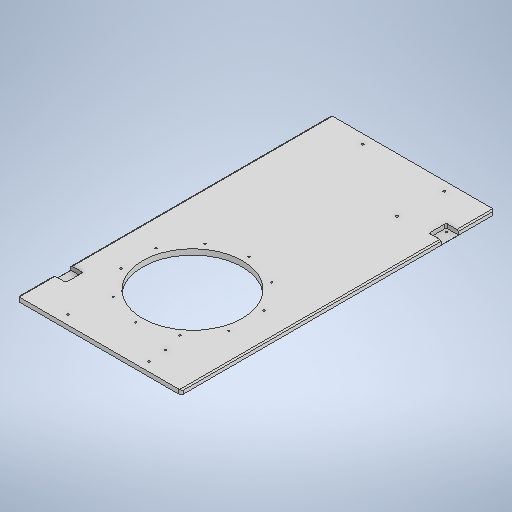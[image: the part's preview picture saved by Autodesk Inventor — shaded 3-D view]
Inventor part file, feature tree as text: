
AUTODESK INVENTOR PART (.ipt)
format: ipt  version: 2025 (Build 290162000, 162)  size: 412,160 bytes
history: native  units: in
note: dims shown in document units (in); Inventor stores cm internally (conversion verified against a paired STEP export)
features: sketch x10, extrude x5, hole x4, chamfer x3, plane x2, fillet x2, pattern_circular x1
ambient origin geometry x8: Origin, YZ Plane, XZ Plane, XY Plane, X Axis, Y Axis, Z Axis, Center Point
bodies: Solid1 (feature_tree)
feature tree (27):
  extrude  "Base Cover"  Depth=27.1654in
  sketch  "Sketch2"  dims[d2=0.4724in d3=0.0in d4=8.0709in]
  extrude  "Cylinder Hole"  Depth=0.4724in
  plane  "Work Plane1"
  hole  "Handle Holes"  [1 undecoded]
  sketch  "Sketch7"  dims[d8=10.6299in d50=5.9055in d55=7.0625in]
  plane  "Work Plane2"
  hole  "Cylinder Mount Holes"  [1 undecoded]
  sketch  "Sketch9"  dims[d57=0.1936in d58=0.1969in d59=0.1575in d60=0.0787in d61=90.0deg d62=0.1969in d63=0.8108in]
  fillet  "Rounded Side Corners"  Radius=7.0625in
  chamfer  "Chamfer1"  Distance=1.063in
  chamfer  "Chamfer2"  Distance=1.063in
  extrude  "Magnet Seats"  Depth=0.315in
  hole  "Magnet Holes"  [1 undecoded]
  chamfer  "Chamfer5"  Distance=3.1102in
  fillet  "Rounded Bottom Corners"  Radius=3.1102in
  extrude  "Extrusion14"  Depth=0.315in
  extrude  "Extrusion15"  Depth=0.0984in TaperAngle=45.0deg
  pattern_circular  "Circular Pattern1"  Angle=45.0deg  [1 undecoded]
  hole  "Hole11"  [1 undecoded]
  sketch  "Sketch1"  dims[d0=14.1732in d1=27.1654in]
  sketch  "Sketch6"  dims[d5=8.6614in d6=0.0in d7=0.0in]
  sketch  "Sketch8"  dims[d56=25.5906in]
  sketch  "Sketch11"  dims[d64=10.3543in]
  sketch  "Sketch18"  dims[d65=10.6299in]
  sketch  "Sketch19"  dims[d68=9.8425in]
  sketch  "Sketch22"  dims[d74=0.1628in d75=0.3937in d76=0.1575in d77=0.0787in d78=90.0deg d79=0.3937in d80=0.8108in d82=1.063in d83=1.063in d84=1.4961in d85=1.4961in d86=3.1102in d87=3.1102in d88=0.1969in d89=0.0984in d90=0.0787in d91=45.0deg d92=0.0984in d93=0.0787in d94=45.0deg d95=0.1181in d96=0.1181in d97=0.3543in d98=0.0in d109=0.748in d110=0.315in d111=0.8661in d112=0.748in d113=0.1299in d114=0.1299in d115=0.1299in d116=0.1299in d118=0.315in d119=0.8661in d120=0.748in d121=0.748in d122=0.1276in d123=0.315in d124=0.1575in d125=0.0787in d126=90.0deg d127=0.315in d128=0.8108in d129=0.0138in d130=0.0787in d131=45.0deg d230=0.2756in d243=0.1378in d244=0.0787in d245=0.3848in d246=0.0in d247=0.1378in d248=0.0787in d249=0.3937in d250=0.0in d278=0.1575in d279=3.937in d280=360.0deg d284=0.1969in d285=0.2362in d286=0.1575in d287=0.0787in d288=90.0deg d289=0.315in d290=0.0in d291=2.3622in d292=3.7213in d293=3.7213in d294=4.7244in d26=0.0394in d27=0.0394in d28=0.0394in d29=0.0059in d30=0.0098in d31=0.0148in d32=0.5635in d33=0.0295in d34=0.8108in d35=0.0025in d36=0.0295in d37=0.0148in d66=0.0197in d67=0.0344in d251=0.0394in d252=0.0394in d253=0.0394in d254=0.0059in d255=0.0098in d256=0.0148in d257=0.5635in d258=0.0295in d259=0.8108in d260=0.0025in d261=0.0295in d262=0.0148in d263=0.0394in d264=0.0394in d265=0.0059in d266=0.0098in d267=0.0148in d268=0.5635in d269=0.0295in d270=0.8108in d271=0.0025in d272=0.0295in d273=0.0148in]
note: 5 required parameter values undecoded (feature->parameter linkage not recoverable at this tier; creation-order binding heuristic only, values carry confidence <= 0.55)
